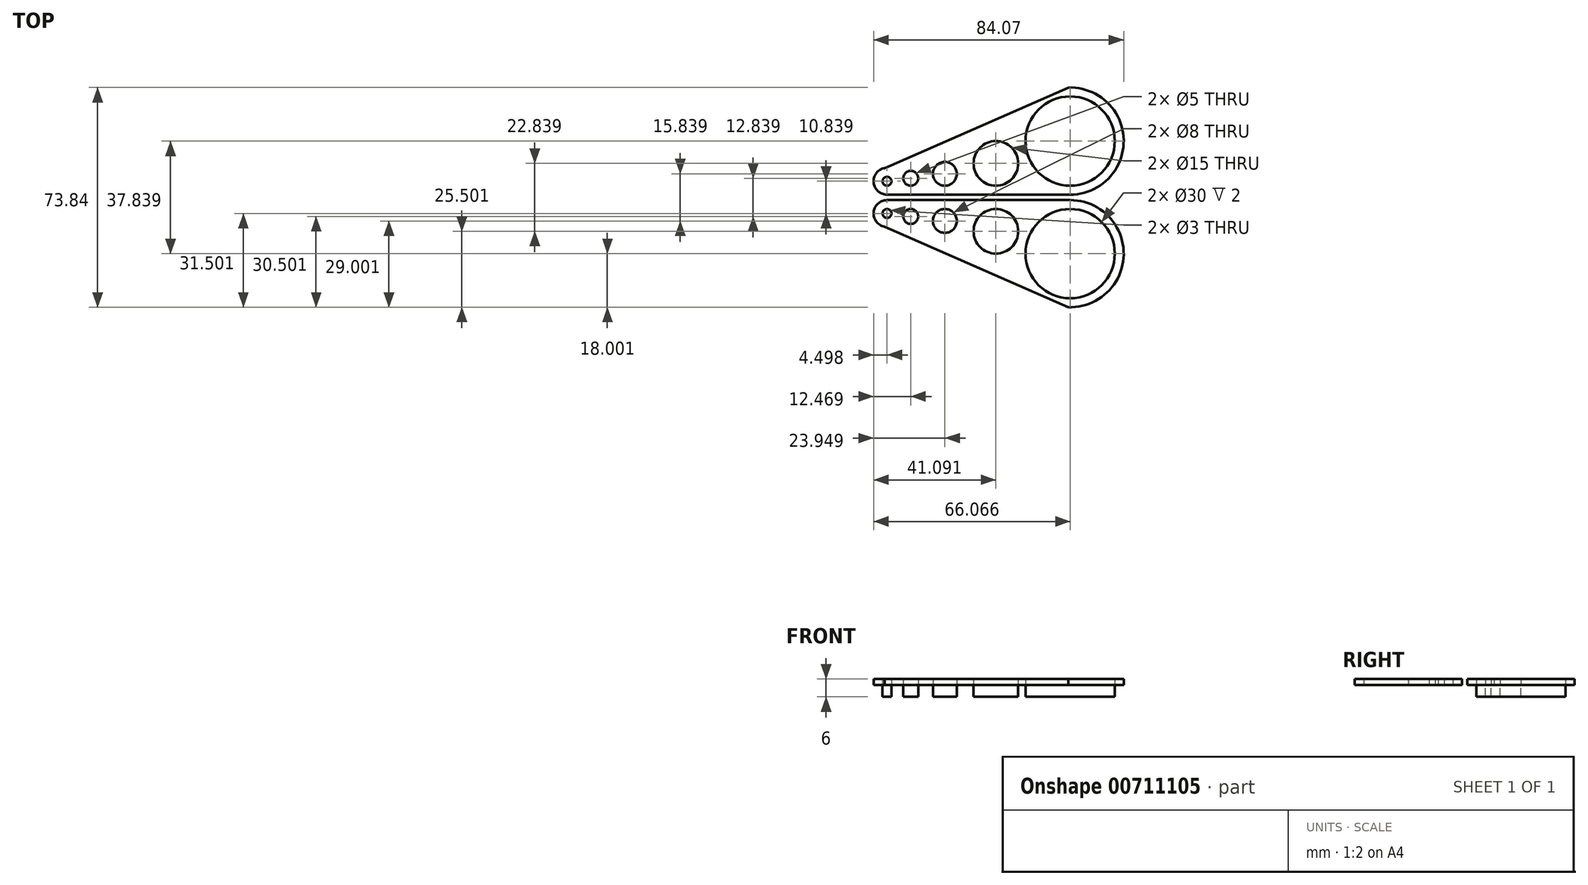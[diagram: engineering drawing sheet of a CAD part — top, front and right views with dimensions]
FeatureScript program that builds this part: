
annotation { "Feature Type Name" : "Feature", "Feature Type Description" : "" }
export const myFeature = defineFeature(function(context is Context, id is Id, definition is map)
    precondition{}
    {
        {
            var Q0;
            Q0=qCreatedBy(makeId("Top.planeOp"),FACE);
            var sketch = newSketch(context, id + "F0", { "sketchPlane" : qUnion([Q0])});
            skPoint(sketch, "E0", {"position": v(0, 0) * mm});
            skCircle(sketch, "E1", {"center": v(-2.33, 6.42) * mm, "radius": 2.5 * mm});
            skCircle(sketch, "E2", {"center": v(9.15, 7.92) * mm, "radius": 4 * mm});
            skCircle(sketch, "E3", {"center": v(26.3, 11.42) * mm, "radius": 7.5 * mm});
            skPoint(sketch, "E4", {"position": v(-10.3, 3.92) * mm});
            skPoint(sketch, "E5", {"position": v(-2.33, 3.92) * mm});
            skPoint(sketch, "E6", {"position": v(9.15, 3.92) * mm});
            skPoint(sketch, "E7", {"position": v(26.3, 3.92) * mm});
            skPoint(sketch, "E8", {"position": v(51.27, 3.92) * mm});
            skPoint(sketch, "E9", {"position": v(-10.3, 6.92) * mm});
            skPoint(sketch, "E10", {"position": v(-2.33, 8.92) * mm});
            skPoint(sketch, "E11", {"position": v(9.15, 11.92) * mm});
            skPoint(sketch, "E12", {"position": v(26.3, 18.92) * mm});
            skPoint(sketch, "E13", {"position": v(51.27, 33.92) * mm});
            skLineSegment(sketch, "E14", {"start": v(-10.3, 6.92) * mm, "end": v(51.27, 33.92) * mm, "construction": true});
            skLineSegment(sketch, "E15", {"start": v(51.27, 3.92) * mm, "end": v(-10.3, 3.92) * mm, "construction": true});
            skArc(sketch, "E16", {"start": v(-10.3, 3.92) * mm, "mid": v(-8.8, 5.42) * mm, "end": v(-10.3, 6.92) * mm});
            skArc(sketch, "E17", {"start": v(-10.3, 6.92) * mm, "mid": v(-11.8, 5.42) * mm, "end": v(-10.3, 3.92) * mm});
            skArc(sketch, "E18", {"start": v(51.27, 33.92) * mm, "mid": v(36.27, 18.92) * mm, "end": v(51.27, 3.92) * mm});
            skArc(sketch, "E19", {"start": v(51.27, 3.92) * mm, "mid": v(66.27, 18.92) * mm, "end": v(51.27, 33.92) * mm});
            skArc(sketch, "E20.0", {"start": v(51.27, 0.92) * mm, "mid": v(69.26, 19.25) * mm, "end": v(50.6, 36.9) * mm});
            skLineSegment(sketch, "E20.1", {"start": v(51.27, 0.92) * mm, "end": v(-10.3, 0.92) * mm});
            skArc(sketch, "E20.2", {"start": v(-11.09, 9.85) * mm, "mid": v(-14.78, 5.02) * mm, "end": v(-10.3, 0.92) * mm});
            skLineSegment(sketch, "E20.3", {"start": v(-11.09, 9.85) * mm, "end": v(50.6, 36.9) * mm});
            skPoint(sketch, "E21.MirrorP", {"position": v(-2.33, -3.92) * mm});
            skPoint(sketch, "E22.MirrorP", {"position": v(26.3, -3.92) * mm});
            skLineSegment(sketch, "E23.MirrorCS", {"start": v(-11.09, -9.85) * mm, "end": v(50.6, -36.9) * mm});
            skArc(sketch, "E24.MirrorCS", {"start": v(-11.09, -9.85) * mm, "mid": v(-14.78, -5.02) * mm, "end": v(-10.3, -0.92) * mm});
            skLineSegment(sketch, "E25.MirrorCS", {"start": v(51.27, -0.92) * mm, "end": v(-10.3, -0.92) * mm});
            skArc(sketch, "E26.MirrorCS", {"start": v(51.27, -0.92) * mm, "mid": v(69.26, -19.25) * mm, "end": v(50.6, -36.9) * mm});
            skPoint(sketch, "E27.MirrorP", {"position": v(26.3, -18.92) * mm});
            skArc(sketch, "E28.MirrorCS", {"start": v(-10.3, -6.92) * mm, "mid": v(-11.8, -5.42) * mm, "end": v(-10.3, -3.92) * mm});
            skCircle(sketch, "E29.MirrorC", {"center": v(-2.33, -6.42) * mm, "radius": 2.5 * mm});
            skLineSegment(sketch, "E30.MirrorCS", {"start": v(-10.3, -6.92) * mm, "end": v(51.27, -33.92) * mm, "construction": true});
            skLineSegment(sketch, "E31.MirrorCS", {"start": v(51.27, -3.92) * mm, "end": v(-10.3, -3.92) * mm, "construction": true});
            skArc(sketch, "E32.MirrorCS", {"start": v(51.27, -3.92) * mm, "mid": v(66.27, -18.92) * mm, "end": v(51.27, -33.92) * mm});
            skPoint(sketch, "E33.MirrorP", {"position": v(-2.33, -8.92) * mm});
            skArc(sketch, "E34.MirrorCS", {"start": v(51.27, -33.92) * mm, "mid": v(36.27, -18.92) * mm, "end": v(51.27, -3.92) * mm});
            skCircle(sketch, "E35.MirrorC", {"center": v(9.15, -7.92) * mm, "radius": 4 * mm});
            skPoint(sketch, "E36.MirrorP", {"position": v(-10.3, -3.92) * mm});
            skPoint(sketch, "E37.MirrorP", {"position": v(9.15, -3.92) * mm});
            skPoint(sketch, "E38.MirrorP", {"position": v(51.27, -3.92) * mm});
            skPoint(sketch, "E39.MirrorP", {"position": v(9.15, -11.92) * mm});
            skPoint(sketch, "E40.MirrorP", {"position": v(51.27, -33.92) * mm});
            skArc(sketch, "E41.MirrorCS", {"start": v(-10.3, -3.92) * mm, "mid": v(-8.8, -5.42) * mm, "end": v(-10.3, -6.92) * mm});
            skPoint(sketch, "E42.MirrorP", {"position": v(-10.3, -6.92) * mm});
            skCircle(sketch, "E43.MirrorC", {"center": v(26.3, -11.42) * mm, "radius": 7.5 * mm});
            skSolve(sketch);
        }
        {
            var Q0;
            Q0=makeQuery(id+"F0.imprint","IMPRINT",FACE,{"disambiguationData":[TD([[makeQuery(id+"F0.imprint","IMPRINT",EDGE,{"derivedFrom":sQuery(id+"F0.wireOp",EDGE,"E23.MirrorCS")}),1.0]])]});
            var Q1;
            Q1=makeQuery(id+"F0.imprint","IMPRINT",FACE,{"disambiguationData":[TD([[makeQuery(id+"F0.imprint","IMPRINT",EDGE,{"derivedFrom":sQuery(id+"F0.wireOp",EDGE,"E1")}),-1.0]])]});
            extrude(context, id + "F1", {"entities" : qUnion([Q0, Q1]), "depth" : 2 * mm, "offsetDistance" : 25 * mm});
        }
        {
            var Q0;
            Q0=makeQuery(id+"F0.imprint","IMPRINT",FACE,{"disambiguationData":[TD([[makeQuery(id+"F0.imprint","IMPRINT",EDGE,{"derivedFrom":sQuery(id+"F0.wireOp",EDGE,"E18")}),1.0]])]});
            var Q1;
            Q1=makeQuery(id+"F0.imprint","IMPRINT",FACE,{"disambiguationData":[TD([[makeQuery(id+"F0.imprint","IMPRINT",EDGE,{"derivedFrom":sQuery(id+"F0.wireOp",EDGE,"E3")}),1.0]])]});
            var Q2;
            Q2=makeQuery(id+"F0.imprint","IMPRINT",FACE,{"disambiguationData":[TD([[makeQuery(id+"F0.imprint","IMPRINT",EDGE,{"derivedFrom":sQuery(id+"F0.wireOp",EDGE,"E2")}),1.0]])]});
            var Q3;
            Q3=makeQuery(id+"F0.imprint","IMPRINT",FACE,{"disambiguationData":[TD([[makeQuery(id+"F0.imprint","IMPRINT",EDGE,{"derivedFrom":sQuery(id+"F0.wireOp",EDGE,"E1")}),1.0]])]});
            var Q4;
            Q4=makeQuery(id+"F0.imprint","IMPRINT",FACE,{"disambiguationData":[TD([[makeQuery(id+"F0.imprint","IMPRINT",EDGE,{"derivedFrom":sQuery(id+"F0.wireOp",EDGE,"E16")}),1.0]])]});
            extrude(context, id + "F2", {"entities" : qUnion([Q0, Q1, Q2, Q3, Q4]), "oppositeDirection" : true, "depth" : 4 * mm, "offsetDistance" : 25 * mm});
        }
    });
